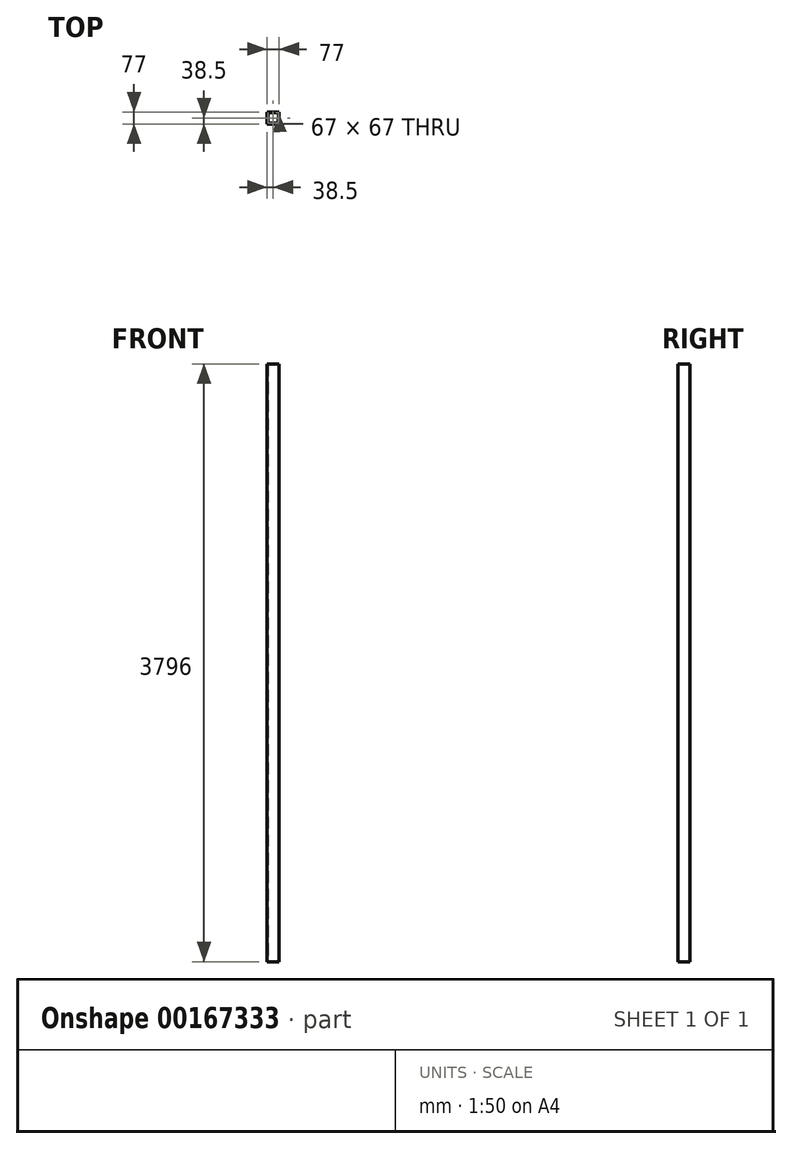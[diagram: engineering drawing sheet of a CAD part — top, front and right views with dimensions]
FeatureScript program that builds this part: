
annotation { "Feature Type Name" : "Feature", "Feature Type Description" : "" }
export const myFeature = defineFeature(function(context is Context, id is Id, definition is map)
    precondition{}
    {
        {
            var Q0;
            Q0=qCreatedBy(makeId("Top.planeOp"),FACE);
            var sketch = newSketch(context, id + "F0", { "sketchPlane" : qUnion([Q0])});
            skLineSegment(sketch, "E0.bottom", {"start": v(0, 0) * mm, "end": v(77, 0) * mm});
            skLineSegment(sketch, "E0.top", {"start": v(0, 77) * mm, "end": v(77, 77) * mm});
            skLineSegment(sketch, "E0.left", {"start": v(0, 0) * mm, "end": v(0, 77) * mm});
            skLineSegment(sketch, "E0.right", {"start": v(77, 0) * mm, "end": v(77, 77) * mm});
            skLineSegment(sketch, "E1.0", {"start": v(5, 5) * mm, "end": v(5, 72) * mm});
            skLineSegment(sketch, "E1.1", {"start": v(5, 5) * mm, "end": v(72, 5) * mm});
            skLineSegment(sketch, "E1.2", {"start": v(72, 5) * mm, "end": v(72, 72) * mm});
            skLineSegment(sketch, "E1.3", {"start": v(5, 72) * mm, "end": v(72, 72) * mm});
            skSolve(sketch);
        }
        {
            var Q0;
            Q0=makeQuery(id+"F0.imprint","IMPRINT",FACE,{"disambiguationData":[TD([[makeQuery(id+"F0.imprint","IMPRINT",EDGE,{"derivedFrom":sQuery(id+"F0.wireOp",EDGE,"E0.bottom")}),1.0]])]});
            extrude(context, id + "F1", {"entities" : qUnion([Q0]), "depth" : 3796 * mm});
        }
    });
